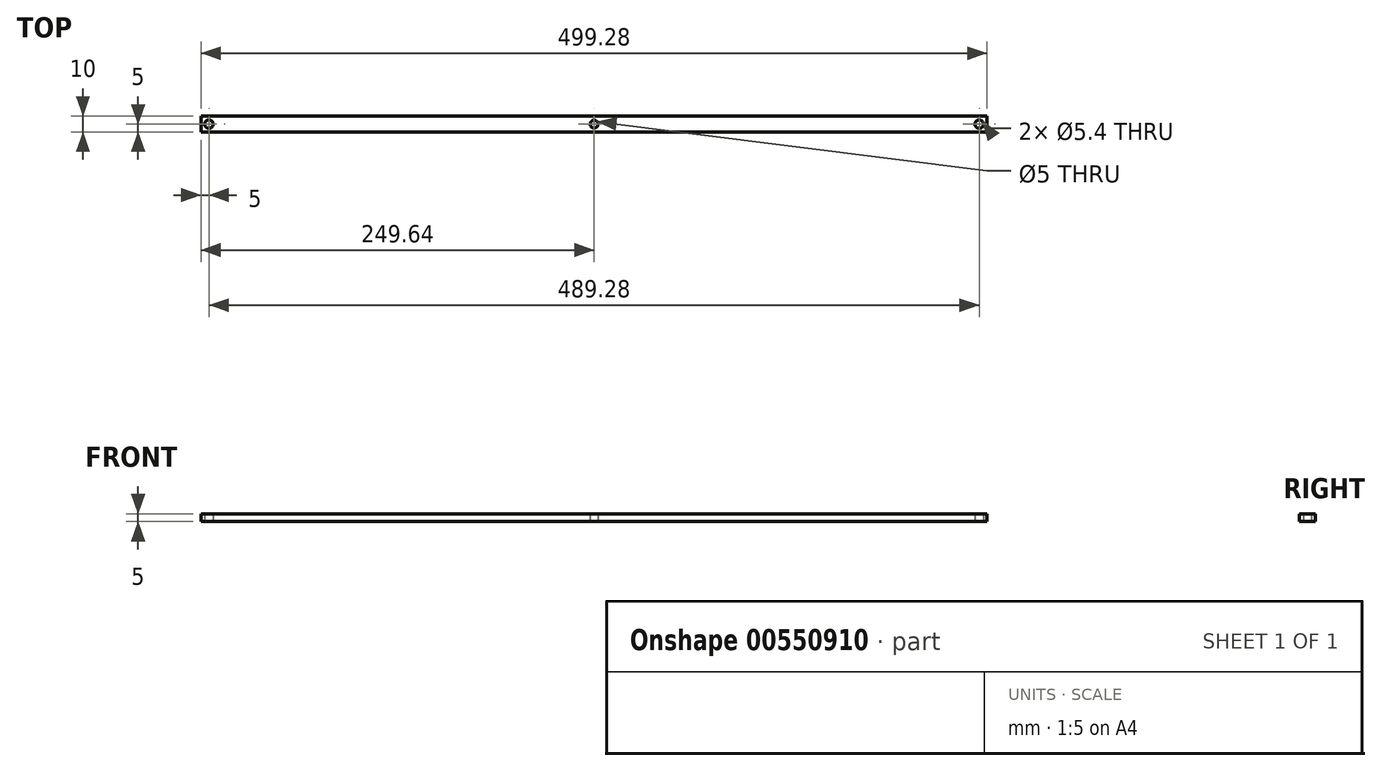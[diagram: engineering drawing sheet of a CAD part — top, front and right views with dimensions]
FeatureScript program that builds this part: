
annotation { "Feature Type Name" : "Feature", "Feature Type Description" : "" }
export const myFeature = defineFeature(function(context is Context, id is Id, definition is map)
    precondition{}
    {
        {
            var Q0;
            Q0=qCreatedBy(makeId("Top.planeOp"),FACE);
            var sketch = newSketch(context, id + "F0", { "sketchPlane" : qUnion([Q0])});
            skLineSegment(sketch, "E0.bottom", {"start": v(-249.64, -5) * mm, "end": v(249.64, -5) * mm});
            skLineSegment(sketch, "E0.top", {"start": v(-249.64, 5) * mm, "end": v(249.64, 5) * mm});
            skLineSegment(sketch, "E0.left", {"start": v(-249.64, -5) * mm, "end": v(-249.64, 5) * mm});
            skLineSegment(sketch, "E0.right", {"start": v(249.64, -5) * mm, "end": v(249.64, 5) * mm});
            skPoint(sketch, "E0.middle", {"position": v(0, 0) * mm});
            skPoint(sketch, "E1", {"position": v(-244.64, 0) * mm});
            skPoint(sketch, "E2", {"position": v(-193.76, 0) * mm});
            skPoint(sketch, "E3", {"position": v(244.64, 0) * mm});
            skSolve(sketch);
        }
        {
            var Q0;
            Q0=makeQuery(id+"F0.imprint","IMPRINT",FACE,{"disambiguationData":[TD([[makeQuery(id+"F0.imprint","IMPRINT",EDGE,{"derivedFrom":sQuery(id+"F0.wireOp",EDGE,"E0.bottom")}),1.0]])]});
            extrude(context, id + "F1", {"entities" : qUnion([Q0]), "depth" : 5 * mm, "offsetDistance" : 25 * mm});
        }
        {
            var Q0;
            Q0=sQuery(id+"F0.wireOp",VERTEX,"E1");
            var Q1;
            Q1=makeQuery(id+"F1.opExtrude","SWEPT_BODY",BODY,{"disambiguationData":[OSD([sQuery(id+"F0.wireOp",EDGE,"E0.bottom"),sQuery(id+"F0.wireOp",EDGE,"E0.top"),sQuery(id+"F0.wireOp",EDGE,"E0.left"),sQuery(id+"F0.wireOp",EDGE,"E0.right")])]});
            hole(context, id + "F2", {"style" : HoleStyle.SIMPLE, "endStyle" : HoleEndStyle.THROUGH, "oppositeDirection" : true, "holeDiameter" : 5.4 * mm, "isTappedThrough" : true, "tappedDepth" : 12 * mm, "tapClearance" : 3, "locations" : qUnion([Q0]), "scope" : qUnion([Q1]), "majorDiameter" : 5 * mm});
        }
        {
            var Q0;
            Q0=sQuery(id+"F0.wireOp",VERTEX,"E0.middle");
            var Q1;
            Q1=makeQuery(id+"F1.opExtrude","SWEPT_BODY",BODY,{"disambiguationData":[OSD([sQuery(id+"F0.wireOp",EDGE,"E0.bottom"),sQuery(id+"F0.wireOp",EDGE,"E0.top"),sQuery(id+"F0.wireOp",EDGE,"E0.left"),sQuery(id+"F0.wireOp",EDGE,"E0.right")])]});
            hole(context, id + "F3", {"style" : HoleStyle.SIMPLE, "endStyle" : HoleEndStyle.THROUGH, "oppositeDirection" : true, "holeDiameter" : 5 * mm, "isTappedThrough" : true, "tappedDepth" : 12 * mm, "tapClearance" : 3, "locations" : qUnion([Q0]), "scope" : qUnion([Q1]), "majorDiameter" : 5 * mm});
        }
        {
            var Q0;
            Q0=sQuery(id+"F0.wireOp",VERTEX,"E3");
            var Q1;
            Q1=makeQuery(id+"F1.opExtrude","SWEPT_BODY",BODY,{"disambiguationData":[OSD([sQuery(id+"F0.wireOp",EDGE,"E0.bottom"),sQuery(id+"F0.wireOp",EDGE,"E0.top"),sQuery(id+"F0.wireOp",EDGE,"E0.left"),sQuery(id+"F0.wireOp",EDGE,"E0.right")])]});
            hole(context, id + "F4", {"style" : HoleStyle.SIMPLE, "endStyle" : HoleEndStyle.THROUGH, "oppositeDirection" : true, "holeDiameter" : 5.4 * mm, "isTappedThrough" : true, "tappedDepth" : 12 * mm, "tapClearance" : 3, "locations" : qUnion([Q0]), "scope" : qUnion([Q1]), "majorDiameter" : 5 * mm});
        }
    });
